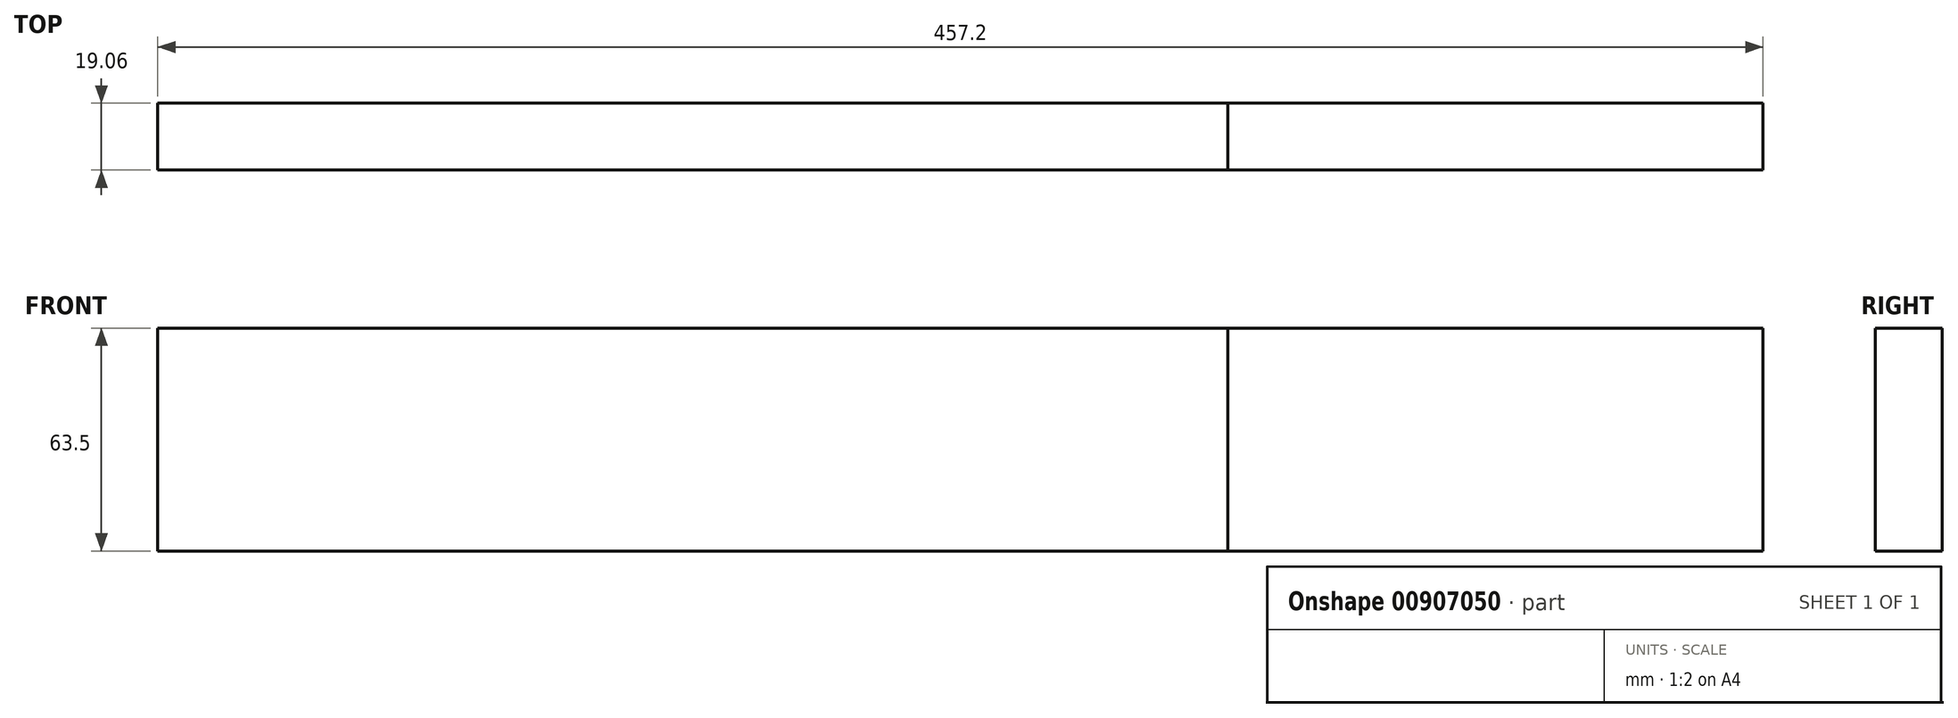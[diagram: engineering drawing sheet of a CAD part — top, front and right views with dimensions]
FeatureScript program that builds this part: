
annotation { "Feature Type Name" : "Feature", "Feature Type Description" : "" }
export const myFeature = defineFeature(function(context is Context, id is Id, definition is map)
    precondition{}
    {
        {
            var Q0;
            Q0=qCreatedBy(makeId("Right.planeOp"),FACE);
            var sketch = newSketch(context, id + "F0", { "sketchPlane" : qUnion([Q0])});
            skLineSegment(sketch, "E0.bottom", {"start": v(-9.52, 31.75) * mm, "end": v(9.53, 31.75) * mm});
            skLineSegment(sketch, "E0.top", {"start": v(-9.53, -31.75) * mm, "end": v(9.52, -31.75) * mm});
            skLineSegment(sketch, "E0.left", {"start": v(-9.52, 31.75) * mm, "end": v(-9.53, -31.75) * mm});
            skLineSegment(sketch, "E0.right", {"start": v(9.53, 31.75) * mm, "end": v(9.52, -31.75) * mm});
            skPoint(sketch, "E0.middle", {"position": v(0, 0) * mm});
            skSolve(sketch);
        }
        {
            var Q0;
            Q0 = qSketchRegion(id + "F0", true);
            extrude(context, id + "F1", {"entities" : qUnion([Q0]), "depth" : 457.2 * mm, "offsetDistance" : 25.4 * mm, "hasSecondDirection" : true, "secondDirectionOppositeDirection" : true, "secondDirectionDepth" : 0 * mm});
        }
        {
            var Q0;
            Q0 = qSketchRegion(id + "F0", true);
            extrude(context, id + "F2", {"entities" : qUnion([Q0]), "depth" : 304.8 * mm, "offsetDistance" : 25.4 * mm});
        }
    });
